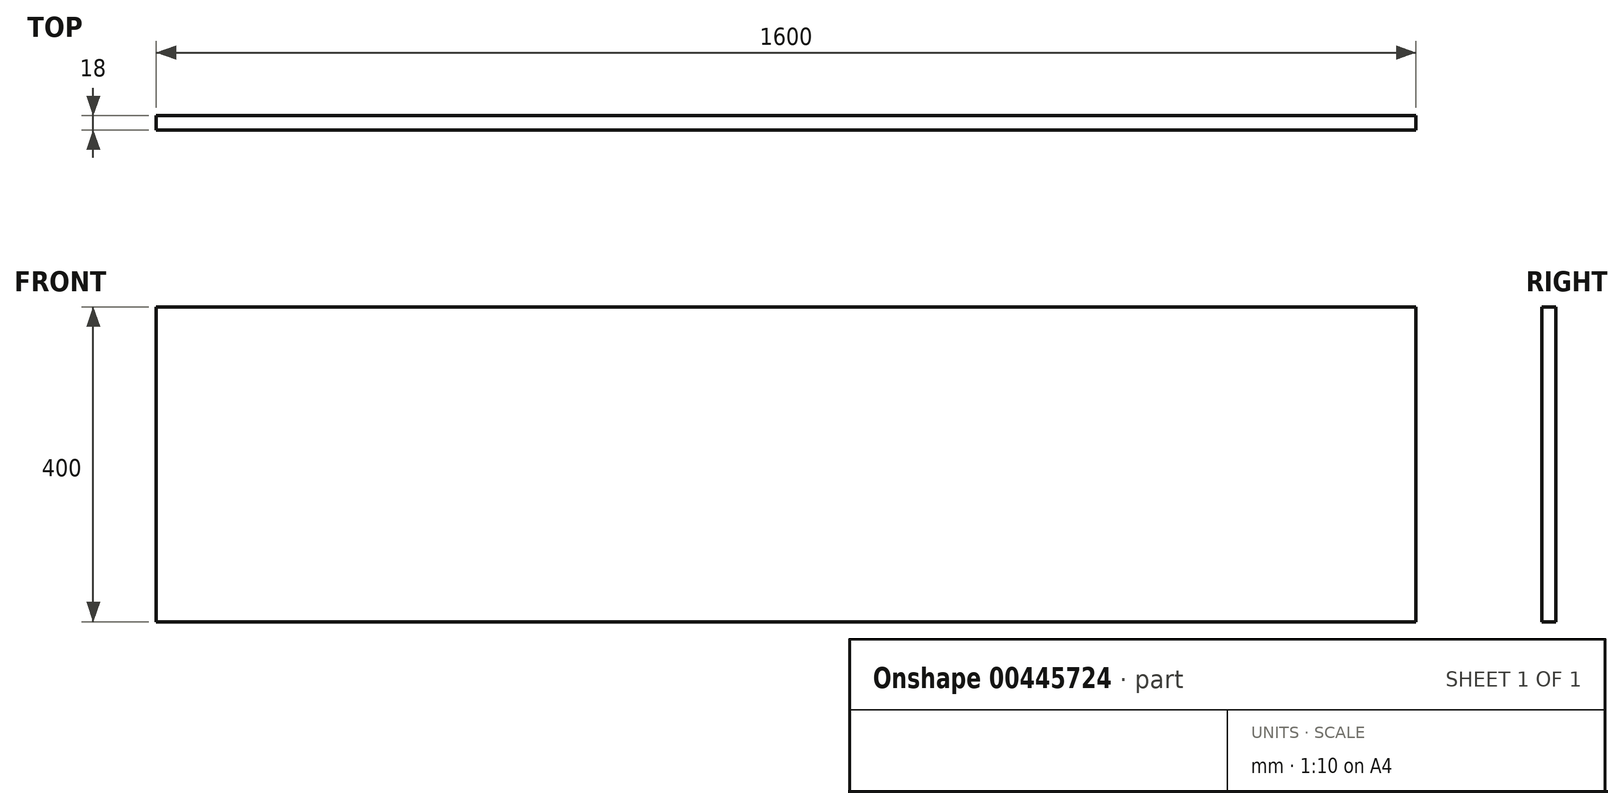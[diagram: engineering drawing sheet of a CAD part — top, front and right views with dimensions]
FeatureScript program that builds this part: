
annotation { "Feature Type Name" : "Feature", "Feature Type Description" : "" }
export const myFeature = defineFeature(function(context is Context, id is Id, definition is map)
    precondition{}
    {
        {
            var Q0;
            Q0=qCreatedBy(makeId("Front.planeOp"),FACE);
            var sketch = newSketch(context, id + "F0", { "sketchPlane" : qUnion([Q0])});
            skLineSegment(sketch, "E0.bottom", {"start": v(0, 0) * mm, "end": v(1600, 0) * mm});
            skLineSegment(sketch, "E0.top", {"start": v(0, -400) * mm, "end": v(1600, -400) * mm});
            skLineSegment(sketch, "E0.left", {"start": v(0, 0) * mm, "end": v(0, -400) * mm});
            skLineSegment(sketch, "E0.right", {"start": v(1600, 0) * mm, "end": v(1600, -400) * mm});
            skSolve(sketch);
        }
        {
            var Q0;
            Q0 = qSketchRegion(id + "F0", true);
            extrude(context, id + "F1", {"entities" : qUnion([Q0]), "depth" : 18 * mm});
        }
    });
